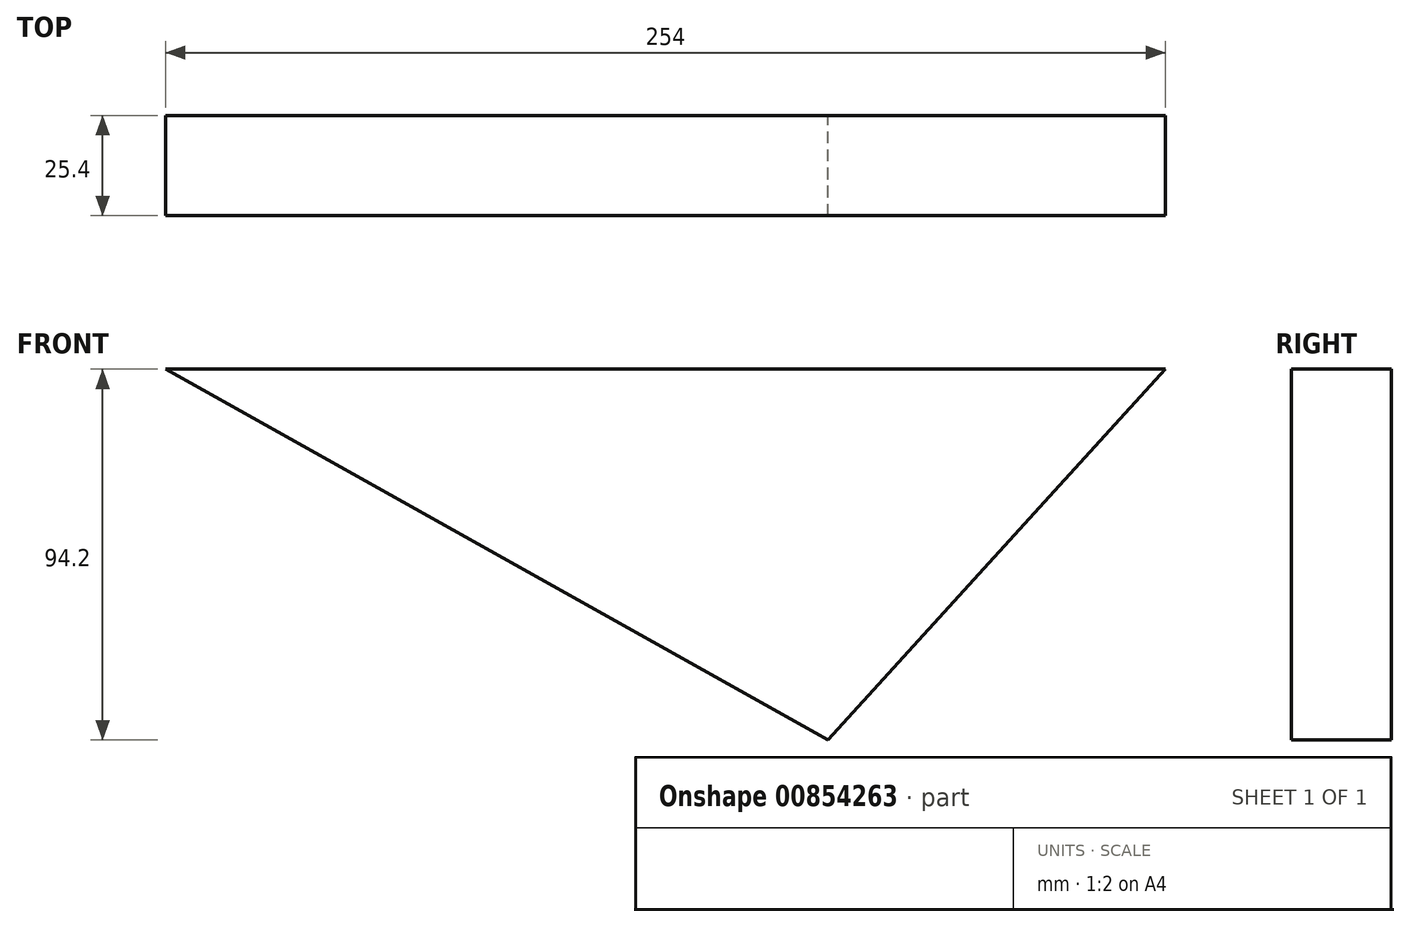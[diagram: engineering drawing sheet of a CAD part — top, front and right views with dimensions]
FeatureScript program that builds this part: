
annotation { "Feature Type Name" : "Feature", "Feature Type Description" : "" }
export const myFeature = defineFeature(function(context is Context, id is Id, definition is map)
    precondition{}
    {
        {
            var Q0;
            Q0=qCreatedBy(makeId("Front.planeOp"),FACE);
            var sketch = newSketch(context, id + "F0", { "sketchPlane" : qUnion([Q0])});
            skLineSegment(sketch, "E0", {"start": v(-83.69, 0) * mm, "end": v(170.31, 0) * mm});
            skLineSegment(sketch, "E1", {"start": v(170.31, 0) * mm, "end": v(84.53, -94.2) * mm});
            skLineSegment(sketch, "E2", {"start": v(84.53, -94.2) * mm, "end": v(-83.69, 0) * mm});
            skSolve(sketch);
        }
        {
            var Q0;
            Q0 = qSketchRegion(id + "F0", true);
            extrude(context, id + "F1", {"entities" : qUnion([Q0]), "depth" : 25.4 * mm, "offsetDistance" : 25.4 * mm});
        }
    });
